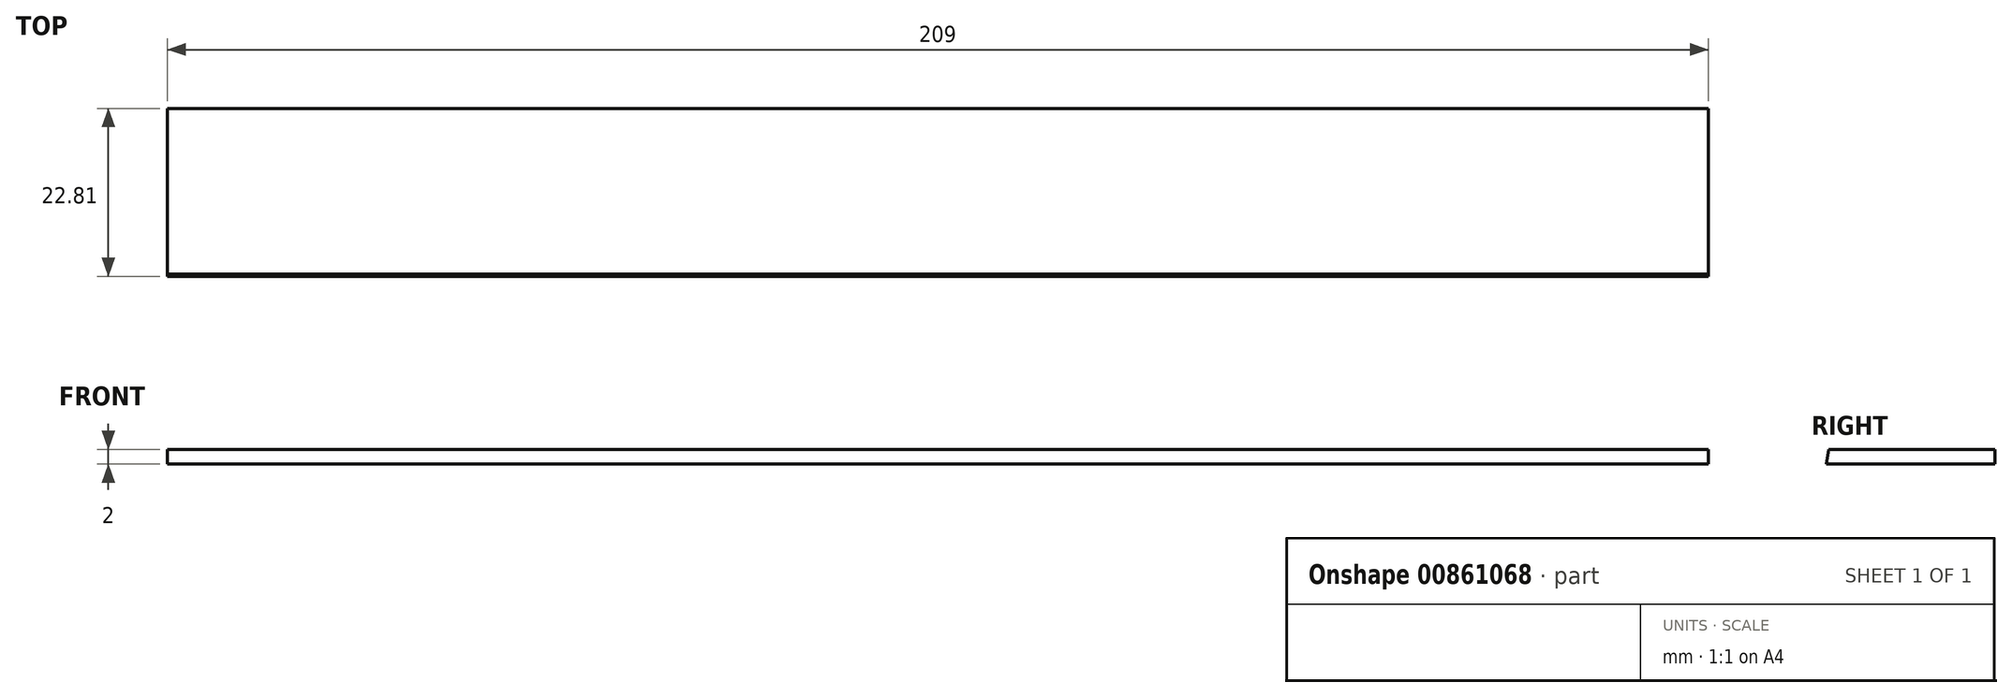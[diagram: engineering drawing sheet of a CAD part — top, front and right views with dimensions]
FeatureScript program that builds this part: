
annotation { "Feature Type Name" : "Feature", "Feature Type Description" : "" }
export const myFeature = defineFeature(function(context is Context, id is Id, definition is map)
    precondition{}
    {
        {
            var Q0;
            Q0=qCreatedBy(makeId("Top.planeOp"),FACE);
            var sketch = newSketch(context, id + "F0", { "sketchPlane" : qUnion([Q0])});
            skPoint(sketch, "E0.middle", {"position": v(0, 0) * mm});
            skPoint(sketch, "E1.visualSharp", {"position": v(-104.5, 11.75) * mm});
            skPoint(sketch, "E2.visualSharp", {"position": v(-104.5, -11.75) * mm});
            skPoint(sketch, "E3.visualSharp", {"position": v(104.5, 11.75) * mm});
            skPoint(sketch, "E4.visualSharp", {"position": v(104.5, -11.75) * mm});
            skLineSegment(sketch, "E5", {"start": v(104.5, 11.75) * mm, "end": v(104.5, -11.75) * mm});
            skLineSegment(sketch, "E6", {"start": v(104.5, -11.75) * mm, "end": v(-104.5, -11.75) * mm});
            skLineSegment(sketch, "E7", {"start": v(-104.5, -11.75) * mm, "end": v(-104.5, 11.75) * mm});
            skLineSegment(sketch, "E8", {"start": v(-104.5, 11.75) * mm, "end": v(104.5, 11.75) * mm});
            skSolve(sketch);
        }
        {
            var Q0;
            Q0=makeQuery(id+"F0.imprint","IMPRINT",FACE,{"disambiguationData":[TD([[makeQuery(id+"F0.imprint","IMPRINT",EDGE,{"derivedFrom":sQuery(id+"F0.wireOp",EDGE,"E5")}),-1.0]])]});
            extrude(context, id + "F1", {"entities" : qUnion([Q0]), "depth" : 2 * mm, "offsetDistance" : 25 * mm});
        }
        {
            var Q0;
            Q0=makeQuery(id+"F1.opExtrude","CAP_EDGE",EDGE,{"disambiguationData":[OSD([sQuery(id+"F0.wireOp",EDGE,"E6")])],"isStart":false});
            chamfer(context, id + "F2", {"entities" : qUnion([Q0]), "chamferType" : ChamferType.TWO_OFFSETS, "width1" : 1 * mm, "oppositeDirection" : false, "width2" : 6.5 * mm, "tangentPropagation" : true});
        }
    });
